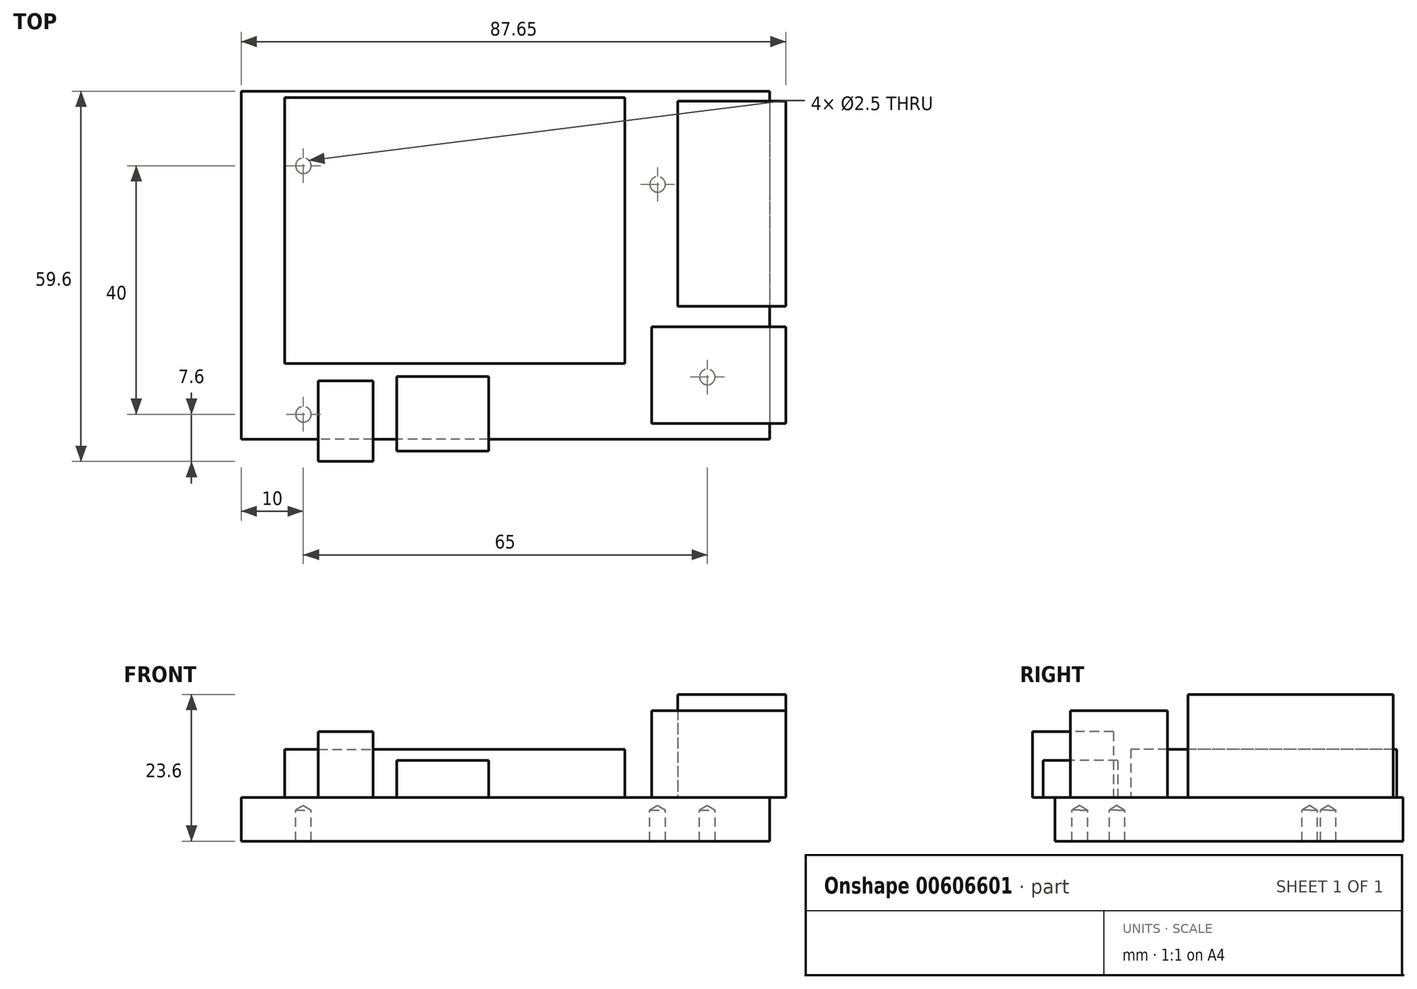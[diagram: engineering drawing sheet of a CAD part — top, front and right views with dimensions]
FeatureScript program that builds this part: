
annotation { "Feature Type Name" : "Feature", "Feature Type Description" : "" }
export const myFeature = defineFeature(function(context is Context, id is Id, definition is map)
    precondition{}
    {
        {
            var Q0;
            Q0=qCreatedBy(makeId("Top.planeOp"),FACE);
            var sketch = newSketch(context, id + "F0", { "sketchPlane" : qUnion([Q0])});
            skLineSegment(sketch, "E0.bottom", {"start": v(42.5, 28) * mm, "end": v(-42.5, 28) * mm});
            skLineSegment(sketch, "E0.top", {"start": v(42.5, -28) * mm, "end": v(-42.5, -28) * mm});
            skLineSegment(sketch, "E0.left", {"start": v(42.5, 28) * mm, "end": v(42.5, -28) * mm});
            skLineSegment(sketch, "E0.right", {"start": v(-42.5, 28) * mm, "end": v(-42.5, -28) * mm});
            skPoint(sketch, "E0.middle", {"position": v(0, 0) * mm});
            skPoint(sketch, "E1", {"position": v(32.5, -18) * mm});
            skPoint(sketch, "E2", {"position": v(24.5, 13) * mm});
            skPoint(sketch, "E3", {"position": v(-32.5, -24) * mm});
            skPoint(sketch, "E4", {"position": v(-32.5, 16) * mm});
            skSolve(sketch);
        }
        {
            var Q0;
            Q0=makeQuery(id+"F0.imprint","IMPRINT",FACE,{"disambiguationData":[TD([[makeQuery(id+"F0.imprint","IMPRINT",EDGE,{"derivedFrom":sQuery(id+"F0.wireOp",EDGE,"E0.bottom")}),1.0]])]});
            extrude(context, id + "F1", {"entities" : qUnion([Q0]), "depth" : 7 * mm, "offsetDistance" : 25 * mm});
        }
        {
            var Q0;
            Q0=makeQuery(id+"F1.opExtrude","CAP_FACE",FACE,{"disambiguationData":[OSD([sQuery(id+"F0.wireOp",EDGE,"E0.bottom"),sQuery(id+"F0.wireOp",EDGE,"E0.top"),sQuery(id+"F0.wireOp",EDGE,"E0.left"),sQuery(id+"F0.wireOp",EDGE,"E0.right")])],"isStart":false});
            var sketch = newSketch(context, id + "F2", { "sketchPlane" : qUnion([Q0])});
            skLineSegment(sketch, "E5.bottom", {"start": v(27.75, -6.6) * mm, "end": v(45.15, -6.6) * mm});
            skLineSegment(sketch, "E5.top", {"start": v(27.75, 26.4) * mm, "end": v(45.15, 26.4) * mm});
            skLineSegment(sketch, "E5.left", {"start": v(27.75, -6.6) * mm, "end": v(27.75, 26.4) * mm});
            skLineSegment(sketch, "E5.right", {"start": v(45.15, -6.6) * mm, "end": v(45.15, 26.4) * mm});
            skLineSegment(sketch, "E6.bottom", {"start": v(23.55, -9.9) * mm, "end": v(45.15, -9.9) * mm});
            skLineSegment(sketch, "E6.top", {"start": v(23.55, -25.5) * mm, "end": v(45.15, -25.5) * mm});
            skLineSegment(sketch, "E6.left", {"start": v(23.55, -9.9) * mm, "end": v(23.55, -25.5) * mm});
            skLineSegment(sketch, "E6.right", {"start": v(45.15, -9.9) * mm, "end": v(45.15, -25.5) * mm});
            skLineSegment(sketch, "E7.bottom", {"start": v(-35.5, 27) * mm, "end": v(19.2, 27) * mm});
            skLineSegment(sketch, "E7.top", {"start": v(-35.5, -15.8) * mm, "end": v(19.2, -15.8) * mm});
            skLineSegment(sketch, "E7.left", {"start": v(-35.5, 27) * mm, "end": v(-35.5, -15.8) * mm});
            skLineSegment(sketch, "E7.right", {"start": v(19.2, 27) * mm, "end": v(19.2, -15.8) * mm});
            skLineSegment(sketch, "E8.bottom", {"start": v(-30.1, -18.6) * mm, "end": v(-21.3, -18.6) * mm});
            skLineSegment(sketch, "E8.top", {"start": v(-30.1, -31.6) * mm, "end": v(-21.3, -31.6) * mm});
            skLineSegment(sketch, "E8.left", {"start": v(-30.1, -18.6) * mm, "end": v(-30.1, -31.6) * mm});
            skLineSegment(sketch, "E8.right", {"start": v(-21.3, -18.6) * mm, "end": v(-21.3, -31.6) * mm});
            skLineSegment(sketch, "E9.bottom", {"start": v(-17.5, -17.9) * mm, "end": v(-2.7, -17.9) * mm});
            skLineSegment(sketch, "E9.top", {"start": v(-17.5, -29.9) * mm, "end": v(-2.7, -29.9) * mm});
            skLineSegment(sketch, "E9.left", {"start": v(-17.5, -17.9) * mm, "end": v(-17.5, -29.9) * mm});
            skLineSegment(sketch, "E9.right", {"start": v(-2.7, -17.9) * mm, "end": v(-2.7, -29.9) * mm});
            skSolve(sketch);
        }
        {
            var Q0;
            {var subQ0=sQuery(id+"F2.wireOp",EDGE,"E5.left");Q0=makeQuery(id+"F2.imprint","IMPRINT",FACE,{"disambiguationData":[TD([[makeQuery(id+"F2.imprint","IMPRINT",EDGE,{"derivedFrom":subQ0}),-1.0]])]});}
            var Q1;
            {var subQ0=sQuery(id+"F2.wireOp",EDGE,"E5.right");Q1=makeQuery(id+"F2.imprint","IMPRINT",FACE,{"disambiguationData":[TD([[makeQuery(id+"F2.imprint","IMPRINT",EDGE,{"derivedFrom":subQ0}),1.0]])]});}
            extrude(context, id + "F3", {"entities" : qUnion([Q0, Q1]), "operationType" : NewBodyOperationType.ADD, "depth" : 16.6 * mm, "offsetDistance" : 25 * mm});
        }
        {
            var Q0;
            {var subQ0=sQuery(id+"F2.wireOp",EDGE,"E6.left");Q0=makeQuery(id+"F2.imprint","IMPRINT",FACE,{"disambiguationData":[TD([[makeQuery(id+"F2.imprint","IMPRINT",EDGE,{"derivedFrom":subQ0}),1.0]])]});}
            var Q1;
            {var subQ0=sQuery(id+"F2.wireOp",EDGE,"E6.right");Q1=makeQuery(id+"F2.imprint","IMPRINT",FACE,{"disambiguationData":[TD([[makeQuery(id+"F2.imprint","IMPRINT",EDGE,{"derivedFrom":subQ0}),-1.0]])]});}
            extrude(context, id + "F4", {"entities" : qUnion([Q0, Q1]), "operationType" : NewBodyOperationType.ADD, "depth" : 14 * mm, "offsetDistance" : 25 * mm});
        }
        {
            var Q0;
            {var subQ0=sQuery(id+"F2.wireOp",EDGE,"E9.bottom");Q0=makeQuery(id+"F2.imprint","IMPRINT",FACE,{"disambiguationData":[TD([[makeQuery(id+"F2.imprint","IMPRINT",EDGE,{"derivedFrom":subQ0}),-1.0]])]});}
            var Q1;
            {var subQ0=sQuery(id+"F2.wireOp",EDGE,"E9.top");Q1=makeQuery(id+"F2.imprint","IMPRINT",FACE,{"disambiguationData":[TD([[makeQuery(id+"F2.imprint","IMPRINT",EDGE,{"derivedFrom":subQ0}),1.0]])]});}
            extrude(context, id + "F5", {"entities" : qUnion([Q0, Q1]), "operationType" : NewBodyOperationType.ADD, "depth" : 6 * mm, "offsetDistance" : 25 * mm});
        }
        {
            var Q0;
            {var subQ0=sQuery(id+"F2.wireOp",EDGE,"E8.bottom");Q0=makeQuery(id+"F2.imprint","IMPRINT",FACE,{"disambiguationData":[TD([[makeQuery(id+"F2.imprint","IMPRINT",EDGE,{"derivedFrom":subQ0}),-1.0]])]});}
            var Q1;
            {var subQ0=sQuery(id+"F2.wireOp",EDGE,"E8.top");Q1=makeQuery(id+"F2.imprint","IMPRINT",FACE,{"disambiguationData":[TD([[makeQuery(id+"F2.imprint","IMPRINT",EDGE,{"derivedFrom":subQ0}),1.0]])]});}
            extrude(context, id + "F6", {"entities" : qUnion([Q0, Q1]), "operationType" : NewBodyOperationType.ADD, "depth" : 10.6 * mm, "offsetDistance" : 25 * mm});
        }
        {
            var Q0;
            Q0=makeQuery(id+"F2.imprint","IMPRINT",FACE,{"disambiguationData":[TD([[makeQuery(id+"F2.imprint","IMPRINT",EDGE,{"derivedFrom":sQuery(id+"F2.wireOp",EDGE,"E7.bottom")}),-1.0]])]});
            extrude(context, id + "F7", {"entities" : qUnion([Q0]), "operationType" : NewBodyOperationType.ADD, "depth" : 7.8 * mm, "offsetDistance" : 25 * mm});
        }
        {
            var Q0;
            Q0=sQuery(id+"F0.wireOp",VERTEX,"E3");
            var Q1;
            Q1=sQuery(id+"F0.wireOp",VERTEX,"E1");
            var Q2;
            Q2=sQuery(id+"F0.wireOp",VERTEX,"E2");
            var Q3;
            Q3=sQuery(id+"F0.wireOp",VERTEX,"E4");
            var Q4;
            Q4=makeQuery(id+"F1.opExtrude","SWEPT_BODY",BODY,{"disambiguationData":[OSD([sQuery(id+"F0.wireOp",EDGE,"E0.bottom"),sQuery(id+"F0.wireOp",EDGE,"E0.top"),sQuery(id+"F0.wireOp",EDGE,"E0.left"),sQuery(id+"F0.wireOp",EDGE,"E0.right")])]});
            hole(context, id + "F8", {"style" : HoleStyle.SIMPLE, "endStyle" : HoleEndStyle.BLIND, "oppositeDirection" : true, "holeDiameter" : 2.5 * mm, "majorDiameter" : 5 * mm, "holeDepth" : 5 * mm, "isTappedThrough" : true, "tappedDepth" : 3.5 * mm, "tapClearance" : 3, "locations" : qUnion([Q0, Q1, Q2, Q3]), "scope" : qUnion([Q4])});
        }
    });
